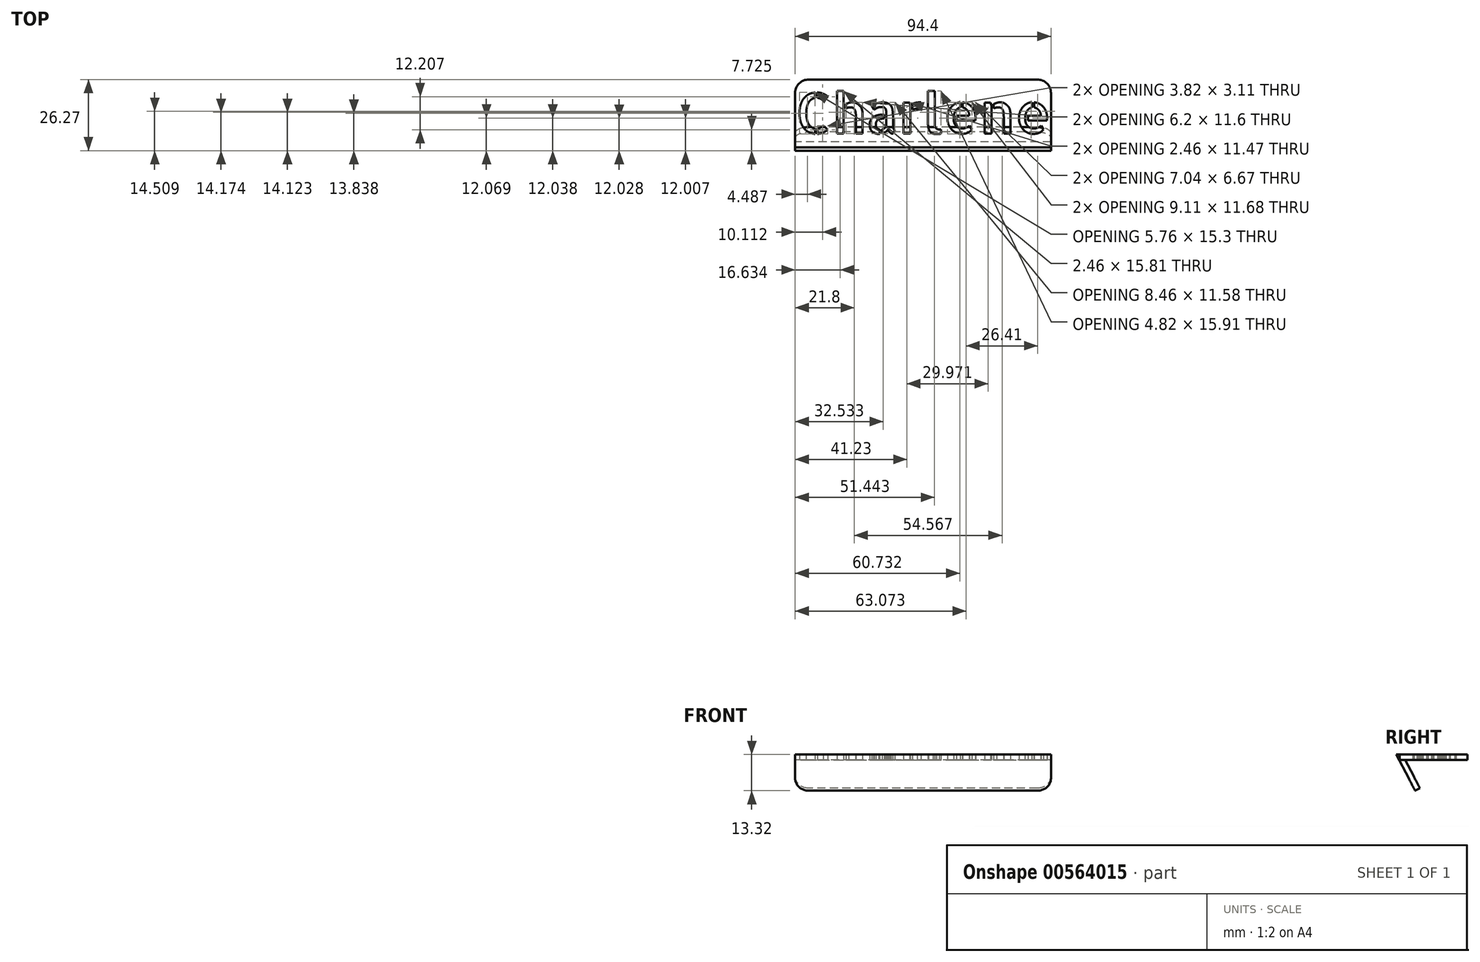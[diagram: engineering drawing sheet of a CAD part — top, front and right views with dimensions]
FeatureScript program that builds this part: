
annotation { "Feature Type Name" : "Feature", "Feature Type Description" : "" }
export const myFeature = defineFeature(function(context is Context, id is Id, definition is map)
    precondition{}
    {
        {
            var Q0;
            Q0=qCreatedBy(makeId("Top.planeOp"),FACE);
            var sketch = newSketch(context, id + "F0", { "sketchPlane" : qUnion([Q0])});
            skLineSegment(sketch, "E0.bottom", {"start": v(-23.58, 12.5) * mm, "end": v(70.82, 12.5) * mm});
            skLineSegment(sketch, "E0.top", {"start": v(-23.58, -12.5) * mm, "end": v(70.82, -12.5) * mm});
            skLineSegment(sketch, "E0.left", {"start": v(-23.58, 12.5) * mm, "end": v(-23.58, -12.5) * mm});
            skLineSegment(sketch, "E0.right", {"start": v(70.82, 12.5) * mm, "end": v(70.82, -12.5) * mm});
            skText(sketch, "E1", { "text": "Charlene", "fontName": "AllertaStencil-Regular.ttf"});
            const initialGuessF0  = {"E1": [-0.02358, -0.0075, 1, 0, 0.015]};
            skSetInitialGuess(sketch, initialGuessF0);
            skSolve(sketch);
        }
        {
            var Q0;
            Q0=makeQuery(id+"F0.imprint","IMPRINT",FACE,{"disambiguationData":[TD([[makeQuery(id+"F0.imprint","IMPRINT",EDGE,{"derivedFrom":sQuery(id+"F0.wireOp",EDGE,"E0.bottom")}),-1.0]])]});
            extrude(context, id + "F1", {"entities" : qUnion([Q0]), "depth" : 2 * mm, "offsetDistance" : 25 * mm});
        }
        {
            var Q0;
            {var subQ0=sQuery(id+"F0.wireOp",EDGE,"E0.left");Q0=makeQuery(id+"FYEOEdhl7jzHk82_2.opBoolean","MERGE",FACE,{"derivedFrom":[makeQuery(id+"F1.opExtrude","SWEPT_FACE",FACE,{"disambiguationData":[OSD([subQ0])]}),makeQuery(id+"FOv1BJgTRWeWuMw_1.opExtrude","CAP_FACE",FACE,{"disambiguationData":[OSD([sQuery(id+"F0.wireOp",EDGE,"E0.bottom"),subQ0,sQuery(id+"Fjco5yBOxZZxTCI_1.wireOp",EDGE,"TpTMtmOo-qoIM-rLEy-p7IH-mKgsBanMGF23"),sQuery(id+"Fjco5yBOxZZxTCI_1.wireOp",EDGE,"Ja6BvVoQ-cpFi-Lcom-cL8s-5xC4kZiynyNl"),sQuery(id+"Fjco5yBOxZZxTCI_1.wireOp",EDGE,"utNyaJ8P-FD6r-AD7x-tpFW-fHytfVhziHLl"),sQuery(id+"Fjco5yBOxZZxTCI_1.wireOp",EDGE,"xGzW29bi-H5H8-ObLh-gdKj-mSPkAtMAUUzO")])],"isStart":true})]});}
            var sketch = newSketch(context, id + "F2", { "sketchPlane" : qUnion([Q0])});
            skLineSegment(sketch, "E2", {"start": v(11.52, 2) * mm, "end": v(5.09, -10.4) * mm});
            skLineSegment(sketch, "E3", {"start": v(5.09, -10.4) * mm, "end": v(6.87, -11.32) * mm});
            skLineSegment(sketch, "E4", {"start": v(6.87, -11.32) * mm, "end": v(13.77, 2) * mm});
            skLineSegment(sketch, "E5", {"start": v(13.77, 2) * mm, "end": v(11.52, 2) * mm});
            skSolve(sketch);
        }
        {
            var Q0;
            {var subQ4=sQuery(id+"F2.wireOp",EDGE,"E3");Q0=makeQuery(id+"F2.imprint","IMPRINT",FACE,{"disambiguationData":[TD([[makeQuery(id+"F2.imprint","IMPRINT",EDGE,{"derivedFrom":subQ4}),1.0]])]});}
            var Q1;
            Q1=makeQuery(id+"F1.opExtrude","SWEPT_FACE",FACE,{"disambiguationData":[OSD([sQuery(id+"F0.wireOp",EDGE,"E0.right")])]});
            extrude(context, id + "F3", {"entities" : qUnion([Q0]), "endBound" : BoundingType.UP_TO_SURFACE, "oppositeDirection" : true, "depth" : 75 * mm, "endBoundEntityFace" : qUnion([Q1]), "offsetDistance" : 25 * mm});
        }
        {
            var Q0;
            Q0=makeQuery(id+"F1.opExtrude","SWEPT_EDGE",EDGE,{"disambiguationData":[OSD([sQuery(id+"F0.wireOp",EDGE,"E0.bottom"),sQuery(id+"F0.wireOp",EDGE,"E0.left")])]});
            var Q1;
            Q1=makeQuery(id+"F1.opExtrude","SWEPT_EDGE",EDGE,{"disambiguationData":[OSD([sQuery(id+"F0.wireOp",EDGE,"E0.bottom"),sQuery(id+"F0.wireOp",EDGE,"E0.right")])]});
            var Q2;
            Q2=makeQuery(id+"F3.opExtrude","CAP_EDGE",EDGE,{"disambiguationData":[OSD([sQuery(id+"F2.wireOp",EDGE,"E3")])],"isStart":false});
            var Q3;
            Q3=makeQuery(id+"F3.opExtrude","CAP_EDGE",EDGE,{"disambiguationData":[OSD([sQuery(id+"F2.wireOp",EDGE,"E3")])],"isStart":true});
            var Q4;
            Q4=makeQuery(id+"F3.opExtrude","TWEAK_EDGE",EDGE,{"derivedFrom":[makeQuery(id+"F1.opExtrude","SWEPT_FACE",FACE,{"disambiguationData":[OSD([sQuery(id+"F0.wireOp",EDGE,"E0.right")])]}),makeQuery(id+"F2.imprint","IMPRINT",EDGE,{"derivedFrom":sQuery(id+"F2.wireOp",EDGE,"E3")})]});
            fillet(context, id + "F4", {"entities" : qUnion([Q0, Q1, Q2, Q3, Q4]), "radius" : 5 * mm, "tangentPropagation" : true, "allowEdgeOverflow" : false});
        }
    });
